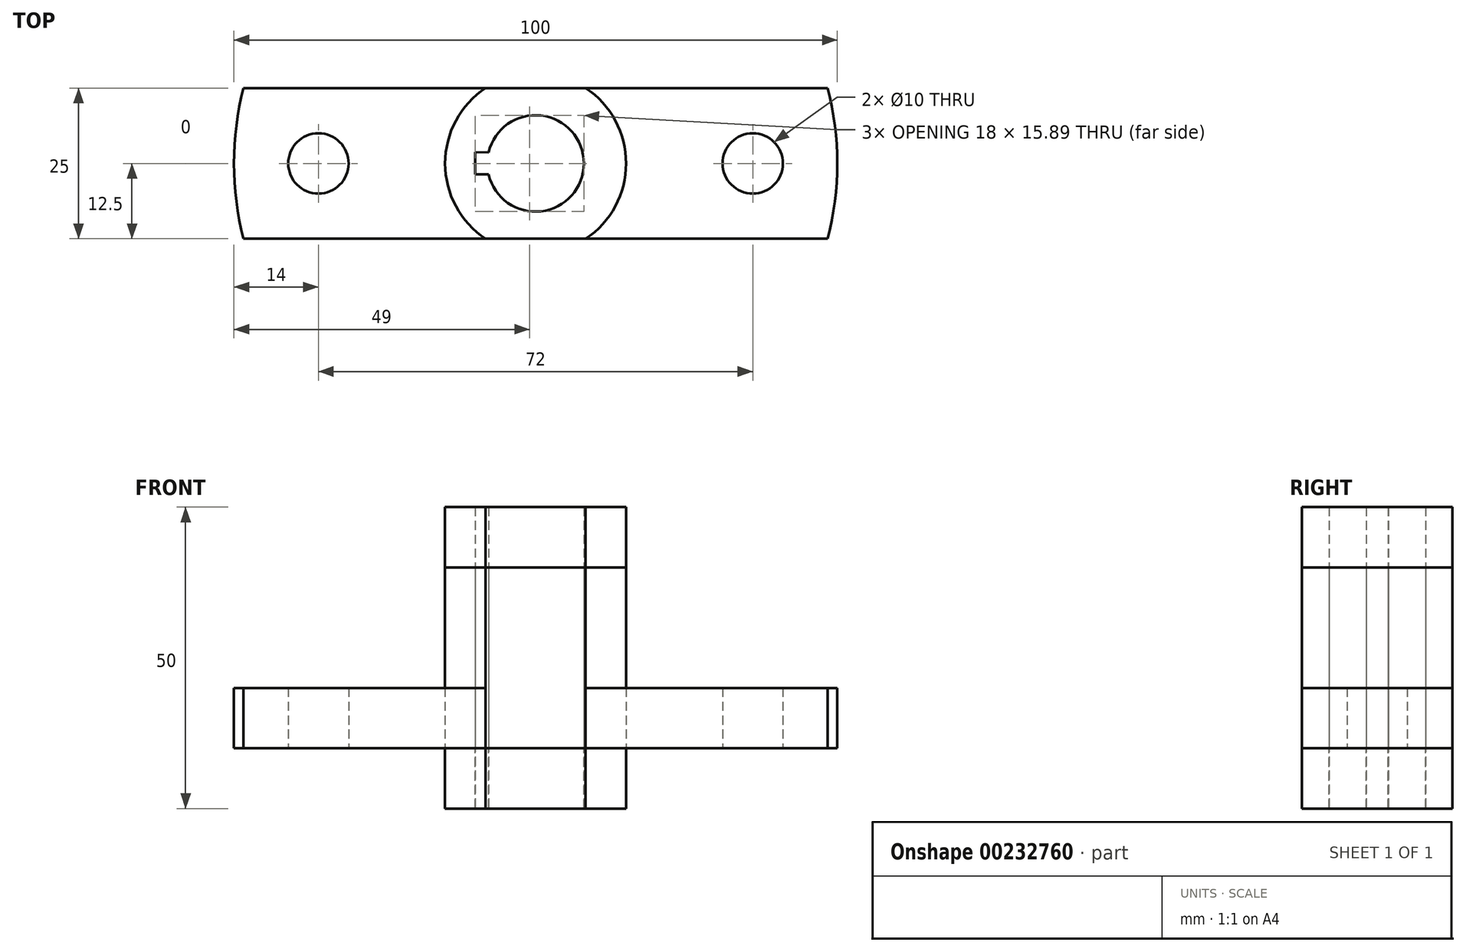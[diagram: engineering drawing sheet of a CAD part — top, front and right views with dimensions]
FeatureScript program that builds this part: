
annotation { "Feature Type Name" : "Feature", "Feature Type Description" : "" }
export const myFeature = defineFeature(function(context is Context, id is Id, definition is map)
    precondition{}
    {
        {
            var Q0;
            Q0=qCreatedBy(makeId("Top.planeOp"),FACE);
            var sketch = newSketch(context, id + "F0", { "sketchPlane" : qUnion([Q0])});
            skArc(sketch, "E0", {"start": v(-48.41, 12.5) * mm, "mid": v(-50, 0) * mm, "end": v(-48.41, -12.5) * mm});
            skArc(sketch, "E1", {"start": v(-7.79, -1.83) * mm, "mid": v(8, 0) * mm, "end": v(-7.79, 1.83) * mm});
            skArc(sketch, "E2", {"start": v(-8.3, 12.5) * mm, "mid": v(-15, 0) * mm, "end": v(-8.3, -12.5) * mm});
            skCircle(sketch, "E3", {"center": v(36, 0) * mm, "radius": 5 * mm});
            skCircle(sketch, "E4", {"center": v(-36, 0) * mm, "radius": 5 * mm});
            skLineSegment(sketch, "E5.left", {"start": v(-10, 1.88) * mm, "end": v(-10, -1.83) * mm});
            skLineSegment(sketch, "E5.right", {"start": v(-7.79, 1.83) * mm, "end": v(-7.79, 1.83) * mm});
            skLineSegment(sketch, "E6.bottom", {"start": v(-48.41, 12.5) * mm, "end": v(48.41, 12.5) * mm});
            skLineSegment(sketch, "E6.top", {"start": v(-48.41, -12.5) * mm, "end": v(48.41, -12.5) * mm});
            skArc(sketch, "E7.trimOffspring", {"start": v(48.41, -12.5) * mm, "mid": v(50, 0) * mm, "end": v(48.41, 12.5) * mm});
            skArc(sketch, "E8.trimOffspring", {"start": v(8.3, -12.5) * mm, "mid": v(15, 0) * mm, "end": v(8.3, 12.5) * mm});
            skLineSegment(sketch, "E9", {"start": v(-7.79, 1.83) * mm, "end": v(-10, 1.88) * mm});
            skLineSegment(sketch, "E10", {"start": v(-7.79, -1.83) * mm, "end": v(-10, -1.83) * mm});
            skSolve(sketch);
        }
        {
            var Q0;
            {var subQ1=sQuery(id+"F0.wireOp",EDGE,"E0");Q0=makeQuery(id+"F0.imprint","IMPRINT",FACE,{"disambiguationData":[TD([[makeQuery(id+"F0.imprint","IMPRINT",EDGE,{"derivedFrom":subQ1}),1.0]])]});}
            var Q1;
            Q1=makeQuery(id+"F0.imprint","IMPRINT",FACE,{"disambiguationData":[TD([[makeQuery(id+"F0.imprint","IMPRINT",EDGE,{"derivedFrom":sQuery(id+"F0.wireOp",EDGE,"E3")}),-1.0]])]});
            extrude(context, id + "F1", {"entities" : qUnion([Q0, Q1]), "depth" : 10 * mm});
        }
        {
            var Q0;
            Q0=makeQuery(id+"F0.imprint","IMPRINT",FACE,{"disambiguationData":[TD([[makeQuery(id+"F0.imprint","IMPRINT",EDGE,{"derivedFrom":sQuery(id+"F0.wireOp",EDGE,"E1")}),-1.0]])]});
            extrude(context, id + "F2", {"entities" : qUnion([Q0]), "operationType" : NewBodyOperationType.ADD, "depth" : 40 * mm});
        }
        {
            var Q0;
            Q0=makeQuery(id+"F0.imprint","IMPRINT",FACE,{"disambiguationData":[TD([[makeQuery(id+"F0.imprint","IMPRINT",EDGE,{"derivedFrom":sQuery(id+"F0.wireOp",EDGE,"E1")}),-1.0]])]});
            extrude(context, id + "F3", {"entities" : qUnion([Q0]), "depth" : 30 * mm});
        }
        {
            var Q0;
            Q0=makeQuery(id+"F0.imprint","IMPRINT",FACE,{"disambiguationData":[TD([[makeQuery(id+"F0.imprint","IMPRINT",EDGE,{"derivedFrom":sQuery(id+"F0.wireOp",EDGE,"E1")}),-1.0]])]});
            extrude(context, id + "F4", {"entities" : qUnion([Q0]), "oppositeDirection" : true, "depth" : 10 * mm});
        }
    });
